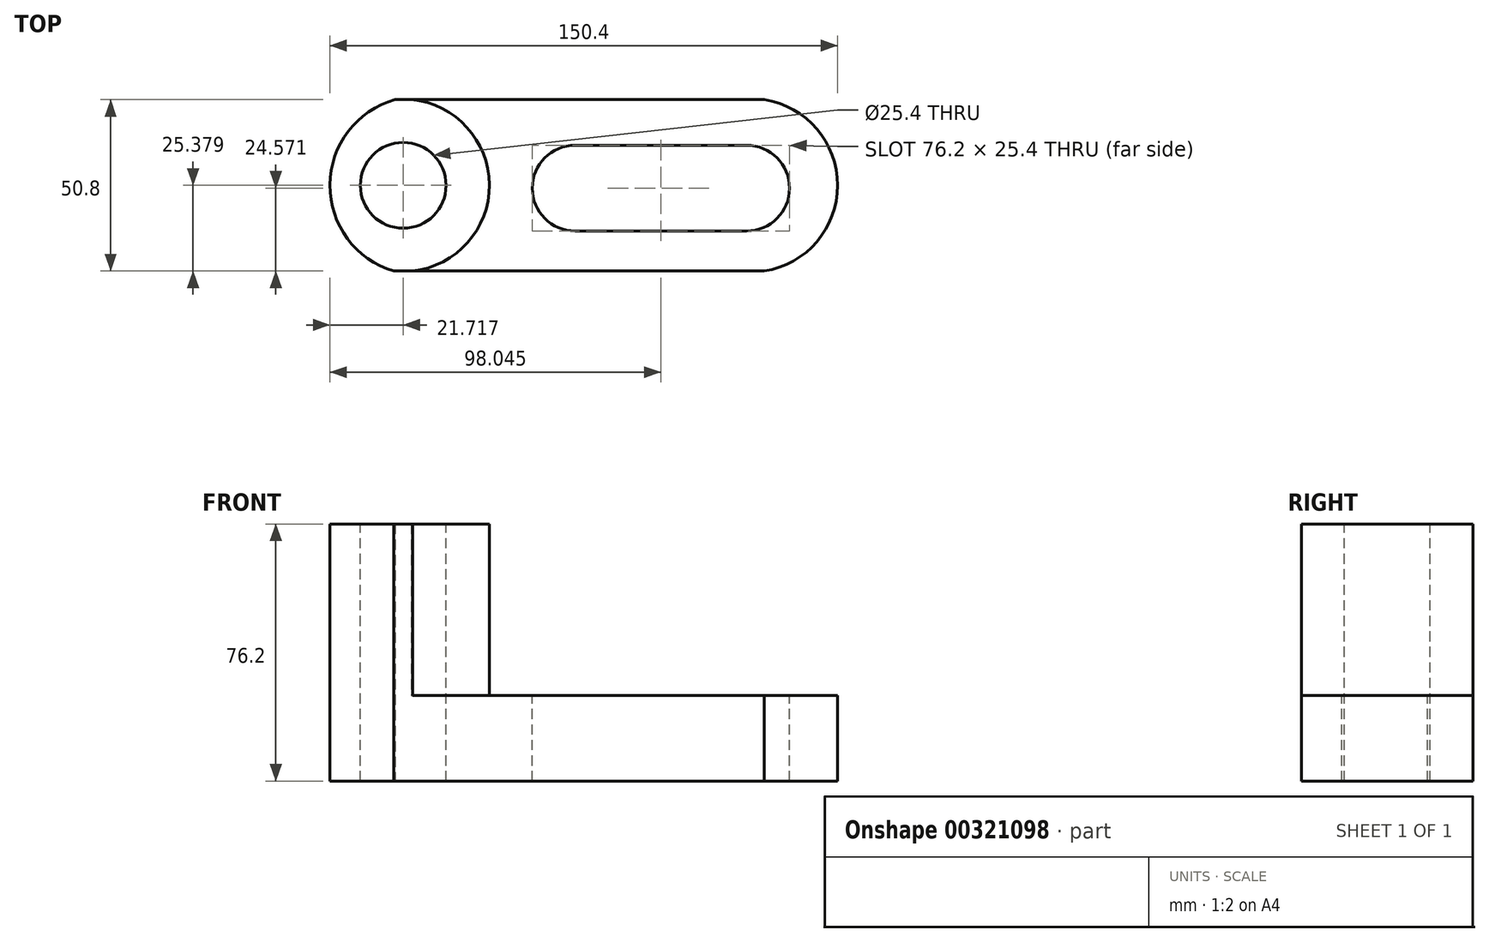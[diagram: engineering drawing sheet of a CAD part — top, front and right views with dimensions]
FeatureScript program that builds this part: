
annotation { "Feature Type Name" : "Feature", "Feature Type Description" : "" }
export const myFeature = defineFeature(function(context is Context, id is Id, definition is map)
    precondition{}
    {
        {
            var Q0;
            Q0=qCreatedBy(makeId("Top.planeOp"),FACE);
            var sketch = newSketch(context, id + "F0", { "sketchPlane" : qUnion([Q0])});
            skLineSegment(sketch, "E0", {"start": v(-54.45, 25.45) * mm, "end": v(54.95, 25.45) * mm});
            skLineSegment(sketch, "E1", {"start": v(-54.76, -25.35) * mm, "end": v(54.95, -25.35) * mm});
            skArc(sketch, "E2", {"start": v(54.95, -25.35) * mm, "mid": v(76.69, 0.05) * mm, "end": v(54.95, 25.45) * mm});
            skArc(sketch, "E3", {"start": v(-54.45, 25.45) * mm, "mid": v(-73.7, 0.16) * mm, "end": v(-54.76, -25.35) * mm});
            skArc(sketch, "E4", {"start": v(-54.76, -25.35) * mm, "mid": v(-26.46, -0.13) * mm, "end": v(-54.45, 25.45) * mm});
            skSolve(sketch);
        }
        {
            var Q0;
            Q0=makeQuery(id+"F0.imprint","IMPRINT",FACE,{"disambiguationData":[TD([[makeQuery(id+"F0.imprint","IMPRINT",EDGE,{"derivedFrom":sQuery(id+"F0.wireOp",EDGE,"E0")}),-1.0]])]});
            extrude(context, id + "F1", {"entities" : qUnion([Q0]), "depth" : 25.4 * mm});
        }
        {
            var Q0;
            {var subQ1=sQuery(id+"F0.wireOp",EDGE,"E3");Q0=makeQuery(id+"F0.imprint","IMPRINT",FACE,{"disambiguationData":[TD([[makeQuery(id+"F0.imprint","IMPRINT",EDGE,{"derivedFrom":subQ1}),1.0]])]});}
            extrude(context, id + "F2", {"entities" : qUnion([Q0]), "operationType" : NewBodyOperationType.ADD, "depth" : 76.2 * mm});
        }
        {
            var Q0;
            Q0=makeQuery(id+"F2.opExtrude","CAP_FACE",FACE,{"disambiguationData":[OSD([sQuery(id+"F0.wireOp",EDGE,"E0"),sQuery(id+"F0.wireOp",EDGE,"E1"),sQuery(id+"F0.wireOp",EDGE,"E3"),sQuery(id+"F0.wireOp",EDGE,"E4")])],"isStart":false});
            var sketch = newSketch(context, id + "F3", { "sketchPlane" : qUnion([Q0])});
            skCircle(sketch, "E5", {"center": v(-52, 0.03) * mm, "radius": 12.7 * mm});
            skSolve(sketch);
        }
        {
            var Q0;
            Q0=makeQuery(id+"F3.imprint","IMPRINT",FACE,{"disambiguationData":[TD([[makeQuery(id+"F3.imprint","IMPRINT",EDGE,{"derivedFrom":sQuery(id+"F3.wireOp",EDGE,"E5")}),1.0]])]});
            extrude(context, id + "F4", {"entities" : qUnion([Q0]), "operationType" : NewBodyOperationType.REMOVE, "endBound" : BoundingType.THROUGH_ALL, "oppositeDirection" : true, "depth" : 25.4 * mm});
        }
        {
            var Q0;
            Q0=makeQuery(id+"F1.opExtrude","CAP_FACE",FACE,{"disambiguationData":[OSD([sQuery(id+"F0.wireOp",EDGE,"E0"),sQuery(id+"F0.wireOp",EDGE,"E1"),sQuery(id+"F0.wireOp",EDGE,"E2"),sQuery(id+"F0.wireOp",EDGE,"E3")])],"isStart":false});
            var sketch = newSketch(context, id + "F5", { "sketchPlane" : qUnion([Q0])});
            skLineSegment(sketch, "E6", {"start": v(-1.06, 11.92) * mm, "end": v(49.74, 11.92) * mm});
            skLineSegment(sketch, "E7", {"start": v(-1.06, -13.48) * mm, "end": v(49.74, -13.48) * mm});
            skArc(sketch, "E8", {"start": v(-1.06, 11.92) * mm, "mid": v(-13.76, -0.78) * mm, "end": v(-1.06, -13.48) * mm});
            skArc(sketch, "E9", {"start": v(49.74, -13.48) * mm, "mid": v(62.44, -0.78) * mm, "end": v(49.74, 11.92) * mm});
            skSolve(sketch);
        }
        {
            var Q0;
            Q0=makeQuery(id+"F5.imprint","IMPRINT",FACE,{"disambiguationData":[TD([[makeQuery(id+"F5.imprint","IMPRINT",EDGE,{"derivedFrom":sQuery(id+"F5.wireOp",EDGE,"E6")}),-1.0]])]});
            extrude(context, id + "F6", {"entities" : qUnion([Q0]), "operationType" : NewBodyOperationType.REMOVE, "endBound" : BoundingType.THROUGH_ALL, "oppositeDirection" : true, "depth" : 25.4 * mm});
        }
    });
